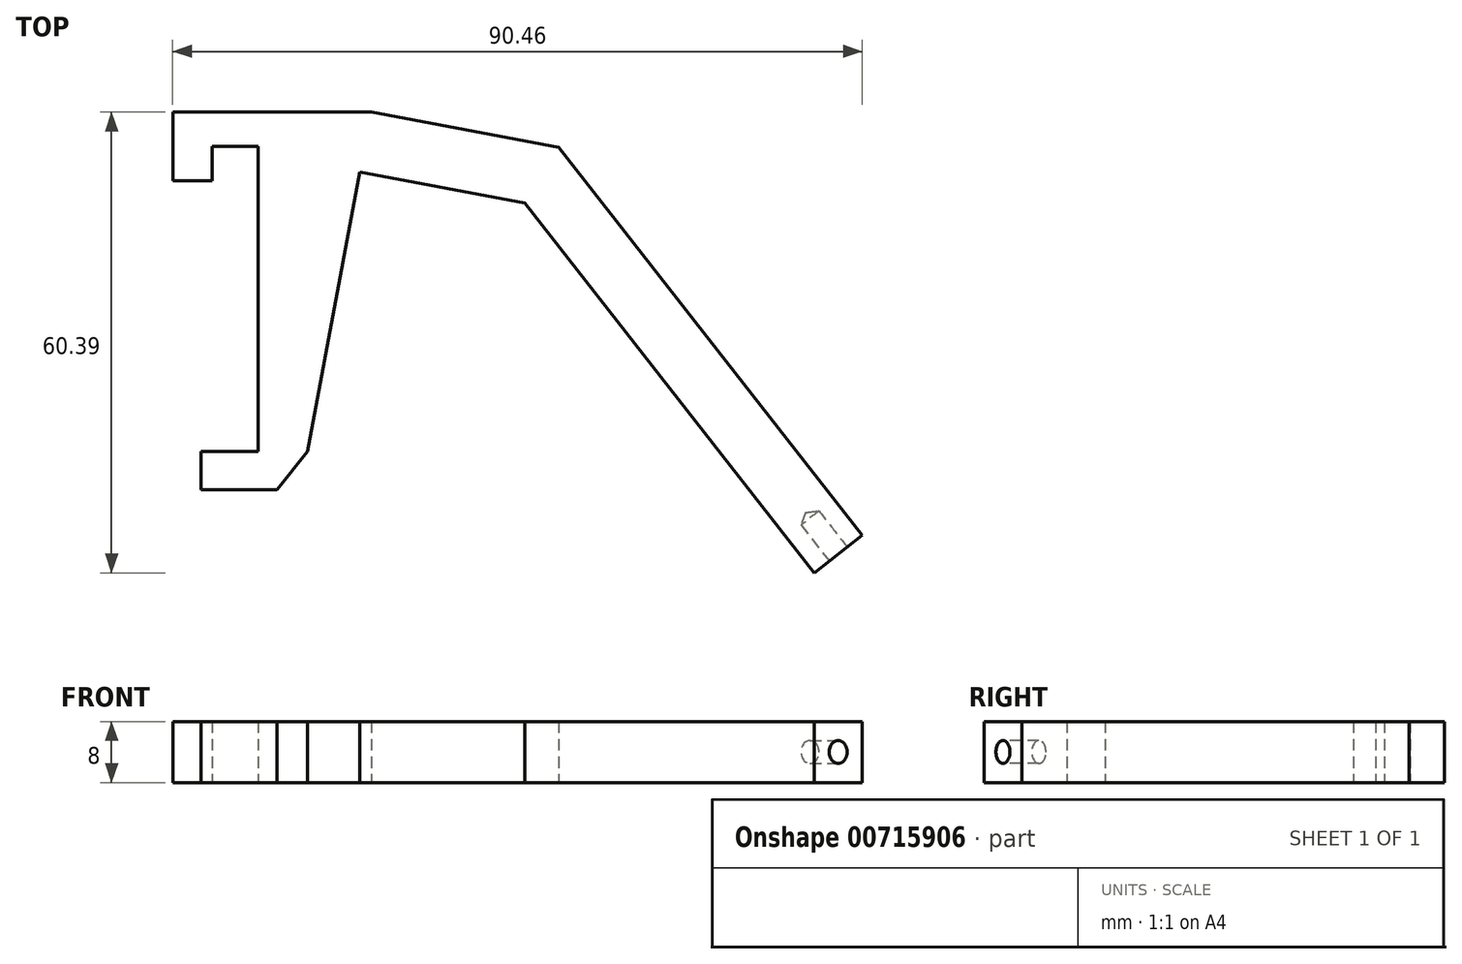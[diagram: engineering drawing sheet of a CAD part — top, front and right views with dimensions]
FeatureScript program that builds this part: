
annotation { "Feature Type Name" : "Feature", "Feature Type Description" : "" }
export const myFeature = defineFeature(function(context is Context, id is Id, definition is map)
    precondition{}
    {
        {
            var Q0;
            Q0=qCreatedBy(makeId("Top.planeOp"),FACE);
            var sketch = newSketch(context, id + "F0", { "sketchPlane" : qUnion([Q0])});
            skLineSegment(sketch, "E0", {"start": v(-35.03, 51.63) * mm, "end": v(-29.03, 51.63) * mm});
            skLineSegment(sketch, "E1", {"start": v(-29.03, 51.63) * mm, "end": v(-29.03, 11.63) * mm});
            skLineSegment(sketch, "E2", {"start": v(-29.03, 11.63) * mm, "end": v(-36.53, 11.63) * mm});
            skLineSegment(sketch, "E3", {"start": v(-36.53, 11.63) * mm, "end": v(-36.53, 6.63) * mm});
            skLineSegment(sketch, "E4", {"start": v(-36.53, 6.63) * mm, "end": v(-26.53, 6.63) * mm});
            skLineSegment(sketch, "E5", {"start": v(-26.53, 6.63) * mm, "end": v(-22.53, 11.63) * mm});
            skLineSegment(sketch, "E6", {"start": v(-35.03, 51.63) * mm, "end": v(-35.03, 47.13) * mm});
            skLineSegment(sketch, "E7", {"start": v(-35.03, 47.13) * mm, "end": v(-40.23, 47.13) * mm});
            skLineSegment(sketch, "E8", {"start": v(-40.23, 47.13) * mm, "end": v(-40.23, 56.13) * mm});
            skLineSegment(sketch, "E9", {"start": v(-29.03, 51.63) * mm, "end": v(-15.03, 51.63) * mm, "construction": true});
            skLineSegment(sketch, "E10", {"start": v(-14.18, 56.13) * mm, "end": v(-40.23, 56.13) * mm});
            skLineSegment(sketch, "E11", {"start": v(-14.18, 56.13) * mm, "end": v(10.39, 51.53) * mm});
            skLineSegment(sketch, "E12", {"start": v(-15.03, 51.63) * mm, "end": v(-8.84, 84.63) * mm, "construction": true});
            skLineSegment(sketch, "E13", {"start": v(-15.03, 51.63) * mm, "end": v(-29.02, -22.98) * mm, "construction": true});
            skLineSegment(sketch, "E14", {"start": v(-22.53, 11.63) * mm, "end": v(-15.03, 51.63) * mm});
            skLineSegment(sketch, "E15", {"start": v(5.95, 44.22) * mm, "end": v(-15.66, 48.27) * mm});
            skLineSegment(sketch, "E16", {"start": v(10.39, 51.53) * mm, "end": v(50.23, 0.67) * mm});
            skLineSegment(sketch, "E17", {"start": v(50.23, 0.67) * mm, "end": v(43.93, -4.26) * mm});
            skLineSegment(sketch, "E18", {"start": v(43.93, -4.26) * mm, "end": v(5.95, 44.22) * mm});
            skSolve(sketch);
        }
        {
            var Q0;
            Q0=qSketchRegion(id+"F0",true);
            extrude(context, id + "F1", {"entities" : qUnion([Q0]), "depth" : 8 * mm, "offsetDistance" : 25 * mm});
        }
        {
            var Q0;
            Q0=makeQuery(id+"F1.opExtrude","SWEPT_FACE",FACE,{"disambiguationData":[OSD([sQuery(id+"F0.wireOp",EDGE,"E17")])]});
            var sketch = newSketch(context, id + "F2", { "sketchPlane" : qUnion([Q0])});
            skPoint(sketch, "E19", {"position": v(35.96, 4) * mm});
            skSolve(sketch);
        }
        {
            var Q0;
            Q0=sQuery(id+"F2.wireOp",VERTEX,"E19");
            var Q1;
            Q1=makeQuery(id+"F1.opExtrude","SWEPT_BODY",BODY,{"disambiguationData":[OSD([sQuery(id+"F0.wireOp",EDGE,"E0"),sQuery(id+"F0.wireOp",EDGE,"E1"),sQuery(id+"F0.wireOp",EDGE,"E2"),sQuery(id+"F0.wireOp",EDGE,"E3"),sQuery(id+"F0.wireOp",EDGE,"E4"),sQuery(id+"F0.wireOp",EDGE,"E5"),sQuery(id+"F0.wireOp",EDGE,"E6"),sQuery(id+"F0.wireOp",EDGE,"E7"),sQuery(id+"F0.wireOp",EDGE,"E8"),sQuery(id+"F0.wireOp",EDGE,"E10"),sQuery(id+"F0.wireOp",EDGE,"E11"),sQuery(id+"F0.wireOp",EDGE,"E14"),sQuery(id+"F0.wireOp",EDGE,"E15"),sQuery(id+"F0.wireOp",EDGE,"E16"),sQuery(id+"F0.wireOp",EDGE,"E17"),sQuery(id+"F0.wireOp",EDGE,"E18")])]});
            hole(context, id + "F3", {"style" : HoleStyle.SIMPLE, "endStyle" : HoleEndStyle.BLIND, "holeDiameter" : 3 * mm, "majorDiameter" : 3 * mm, "holeDepth" : 6 * mm, "isTappedThrough" : true, "tappedDepth" : 12 * mm, "tapClearance" : 3, "locations" : qUnion([Q0]), "scope" : qUnion([Q1])});
        }
    });
